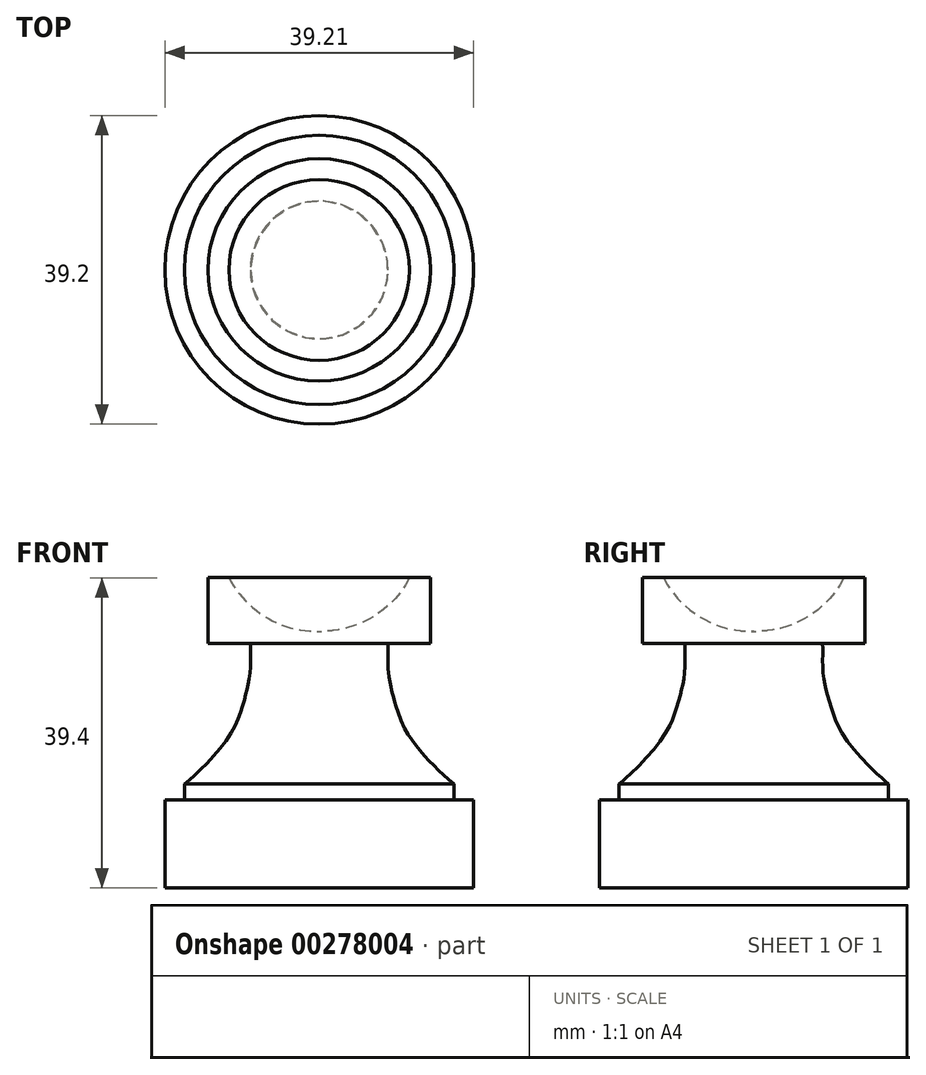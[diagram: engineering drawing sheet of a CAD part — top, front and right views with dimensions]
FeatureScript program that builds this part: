
annotation { "Feature Type Name" : "Feature", "Feature Type Description" : "" }
export const myFeature = defineFeature(function(context is Context, id is Id, definition is map)
    precondition{}
    {
        {
            var Q0;
            Q0=qCreatedBy(makeId("Front.planeOp"),FACE);
            var sketch = newSketch(context, id + "F0", { "sketchPlane" : qUnion([Q0])});
            skLineSegment(sketch, "E0", {"start": v(41.09, 4.34) * mm, "end": v(41.09, 62.15) * mm});
            skLineSegment(sketch, "E1", {"start": v(41.09, 4.34) * mm, "end": v(21.48, 4.34) * mm});
            skLineSegment(sketch, "E2", {"start": v(29.6, 43.74) * mm, "end": v(26.96, 43.74) * mm});
            skLineSegment(sketch, "E3", {"start": v(26.96, 43.74) * mm, "end": v(26.96, 35.4) * mm});
            skLineSegment(sketch, "E4", {"start": v(26.96, 35.4) * mm, "end": v(32.34, 35.4) * mm});
            skLineSegment(sketch, "E5", {"start": v(21.48, 4.34) * mm, "end": v(21.48, 15.52) * mm});
            skLineSegment(sketch, "E6", {"start": v(21.48, 15.52) * mm, "end": v(23.97, 15.52) * mm});
            skLineSegment(sketch, "E7", {"start": v(23.97, 15.52) * mm, "end": v(23.97, 17.56) * mm});
            skFitSpline(sketch, "E8", {"points": [v(23.97, 17.56) * mm, v(25.48, 18.86) * mm, v(28.05, 21.53) * mm, v(30.25, 24.61) * mm, v(31.13, 26.77) * mm, v(31.64, 28.42) * mm, v(31.93, 29.6) * mm, v(32.19, 30.84) * mm, v(32.33, 32.41) * mm, v(32.33, 34.17) * mm, v(32.34, 35.4) * mm], "startDerivative": vector(14.18, 11.58) * mm, "endDerivative": vector(0.23, 14.78) * mm});
            skArc(sketch, "E9", {"start": v(41.09, 62.15) * mm, "mid": v(30.1, 56.22) * mm, "end": v(29.6, 43.74) * mm});
            skSolve(sketch);
        }
        {
            var Q0;
            Q0=makeQuery(id+"F0.imprint","IMPRINT",FACE,{"disambiguationData":[TD([[makeQuery(id+"F0.imprint","IMPRINT",EDGE,{"derivedFrom":sQuery(id+"F0.wireOp",EDGE,"E0")}),1.0]])]});
            var Q1;
            Q1=sQuery(id+"F0.wireOp",EDGE,"E0");
            revolve(context, id + "F1", {"entities" : qUnion([Q0]), "axis" : qUnion([Q1]), "revolveType" : RevolveType.FULL});
        }
    });
